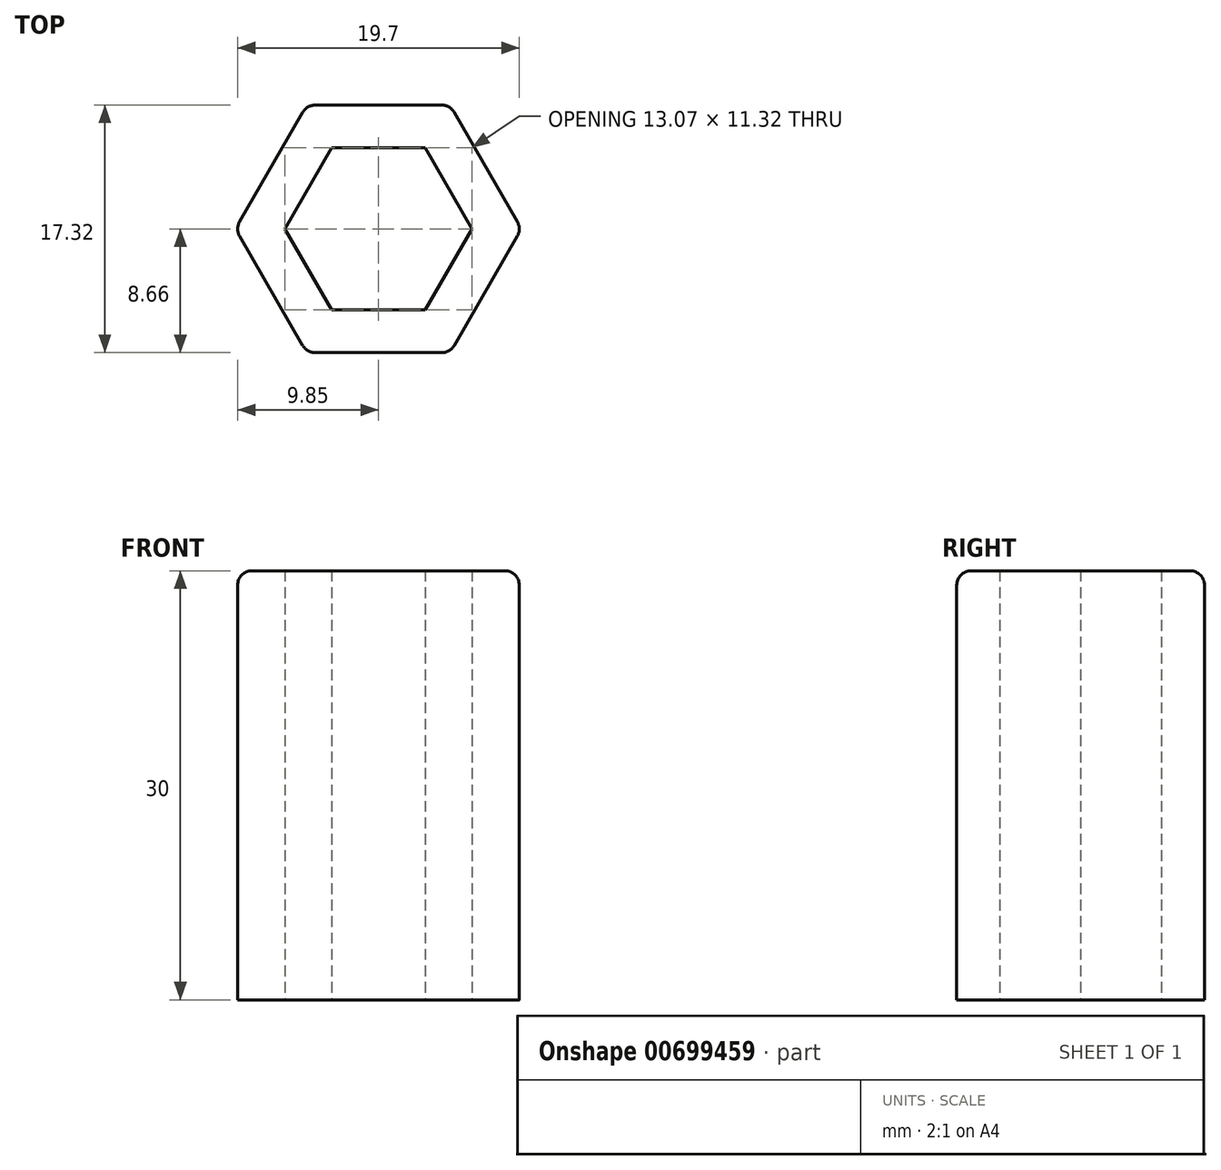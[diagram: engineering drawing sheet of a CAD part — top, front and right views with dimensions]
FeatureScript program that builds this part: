
annotation { "Feature Type Name" : "Feature", "Feature Type Description" : "" }
export const myFeature = defineFeature(function(context is Context, id is Id, definition is map)
    precondition{}
    {
        {
            var Q0;
            Q0=qCreatedBy(makeId("Top.planeOp"),FACE);
            var sketch = newSketch(context, id + "F0", { "sketchPlane" : qUnion([Q0])});
            skLineSegment(sketch, "E0.bottom", {"start": v(10, 10) * mm, "end": v(-10, 10) * mm, "construction": true});
            skLineSegment(sketch, "E0.top", {"start": v(10, -10) * mm, "end": v(-10, -10) * mm, "construction": true});
            skLineSegment(sketch, "E0.left", {"start": v(10, 10) * mm, "end": v(10, -10) * mm, "construction": true});
            skLineSegment(sketch, "E0.right", {"start": v(-10, 10) * mm, "end": v(-10, -10) * mm, "construction": true});
            skPoint(sketch, "E0.middle", {"position": v(0, 0) * mm});
            skCircle(sketch, "E1.cCircle", {"center": v(0, 0) * mm, "radius": 8.66 * mm, "construction": true});
            skLineSegment(sketch, "E1.0", {"start": v(5, 8.66) * mm, "end": v(10, 0) * mm});
            skLineSegment(sketch, "E1.1", {"start": v(10, 0) * mm, "end": v(5, -8.66) * mm});
            skLineSegment(sketch, "E1.2", {"start": v(5, -8.66) * mm, "end": v(-5, -8.66) * mm});
            skLineSegment(sketch, "E1.3", {"start": v(-5, -8.66) * mm, "end": v(-10, 0) * mm});
            skLineSegment(sketch, "E1.4", {"start": v(-10, 0) * mm, "end": v(-5, 8.66) * mm});
            skLineSegment(sketch, "E1.5", {"start": v(-5, 8.66) * mm, "end": v(5, 8.66) * mm});
            skPoint(sketch, "E1.0.midPoint", {"position": v(7.5, 4.33) * mm});
            skLineSegment(sketch, "E2.0", {"start": v(-3.27, -5.66) * mm, "end": v(-6.54, 0) * mm});
            skLineSegment(sketch, "E2.1", {"start": v(-3.27, 5.66) * mm, "end": v(3.27, 5.66) * mm});
            skLineSegment(sketch, "E2.2", {"start": v(3.27, 5.66) * mm, "end": v(6.54, 0) * mm});
            skLineSegment(sketch, "E2.3", {"start": v(-6.54, 0) * mm, "end": v(-3.27, 5.66) * mm});
            skLineSegment(sketch, "E2.4", {"start": v(6.54, 0) * mm, "end": v(3.27, -5.66) * mm});
            skLineSegment(sketch, "E2.5", {"start": v(3.27, -5.66) * mm, "end": v(-3.27, -5.66) * mm});
            skSolve(sketch);
        }
        {
            var Q0;
            Q0=qSketchRegion(id+"F0",true);
            extrude(context, id + "F1", {"entities" : qUnion([Q0]), "depth" : 30 * mm, "offsetDistance" : 25 * mm});
        }
        {
            var Q0;
            Q0=makeQuery(id+"F1.opExtrude","SWEPT_EDGE",EDGE,{"disambiguationData":[OSD([sQuery(id+"F0.wireOp",EDGE,"E1.2"),sQuery(id+"F0.wireOp",EDGE,"E1.3")])]});
            var Q1;
            Q1=makeQuery(id+"F1.opExtrude","CAP_EDGE",EDGE,{"disambiguationData":[OSD([sQuery(id+"F0.wireOp",EDGE,"E1.2")])],"isStart":false});
            var Q2;
            Q2=makeQuery(id+"F1.opExtrude","SWEPT_EDGE",EDGE,{"disambiguationData":[OSD([sQuery(id+"F0.wireOp",EDGE,"E1.1"),sQuery(id+"F0.wireOp",EDGE,"E1.2")])]});
            var Q3;
            Q3=makeQuery(id+"F1.opExtrude","CAP_EDGE",EDGE,{"disambiguationData":[OSD([sQuery(id+"F0.wireOp",EDGE,"E1.1")])],"isStart":false});
            var Q4;
            Q4=makeQuery(id+"F1.opExtrude","SWEPT_EDGE",EDGE,{"disambiguationData":[OSD([sQuery(id+"F0.wireOp",EDGE,"E1.0"),sQuery(id+"F0.wireOp",EDGE,"E1.1")])]});
            var Q5;
            Q5=makeQuery(id+"F1.opExtrude","CAP_EDGE",EDGE,{"disambiguationData":[OSD([sQuery(id+"F0.wireOp",EDGE,"E1.0")])],"isStart":false});
            var Q6;
            Q6=makeQuery(id+"F1.opExtrude","SWEPT_EDGE",EDGE,{"disambiguationData":[OSD([sQuery(id+"F0.wireOp",EDGE,"E1.0"),sQuery(id+"F0.wireOp",EDGE,"E1.5")])]});
            var Q7;
            Q7=makeQuery(id+"F1.opExtrude","CAP_EDGE",EDGE,{"disambiguationData":[OSD([sQuery(id+"F0.wireOp",EDGE,"E1.5")])],"isStart":false});
            var Q8;
            Q8=makeQuery(id+"F1.opExtrude","SWEPT_EDGE",EDGE,{"disambiguationData":[OSD([sQuery(id+"F0.wireOp",EDGE,"E1.4"),sQuery(id+"F0.wireOp",EDGE,"E1.5")])]});
            var Q9;
            Q9=makeQuery(id+"F1.opExtrude","CAP_EDGE",EDGE,{"disambiguationData":[OSD([sQuery(id+"F0.wireOp",EDGE,"E1.4")])],"isStart":false});
            var Q10;
            Q10=makeQuery(id+"F1.opExtrude","SWEPT_EDGE",EDGE,{"disambiguationData":[OSD([sQuery(id+"F0.wireOp",EDGE,"E1.3"),sQuery(id+"F0.wireOp",EDGE,"E1.4")])]});
            var Q11;
            Q11=makeQuery(id+"F1.opExtrude","CAP_EDGE",EDGE,{"disambiguationData":[OSD([sQuery(id+"F0.wireOp",EDGE,"E1.3")])],"isStart":false});
            fillet(context, id + "F2", {"entities" : qUnion([Q0, Q1, Q2, Q3, Q4, Q5, Q6, Q7, Q8, Q9, Q10, Q11]), "radius" : 1 * mm, "tangentPropagation" : true, "allowEdgeOverflow" : false});
        }
    });
